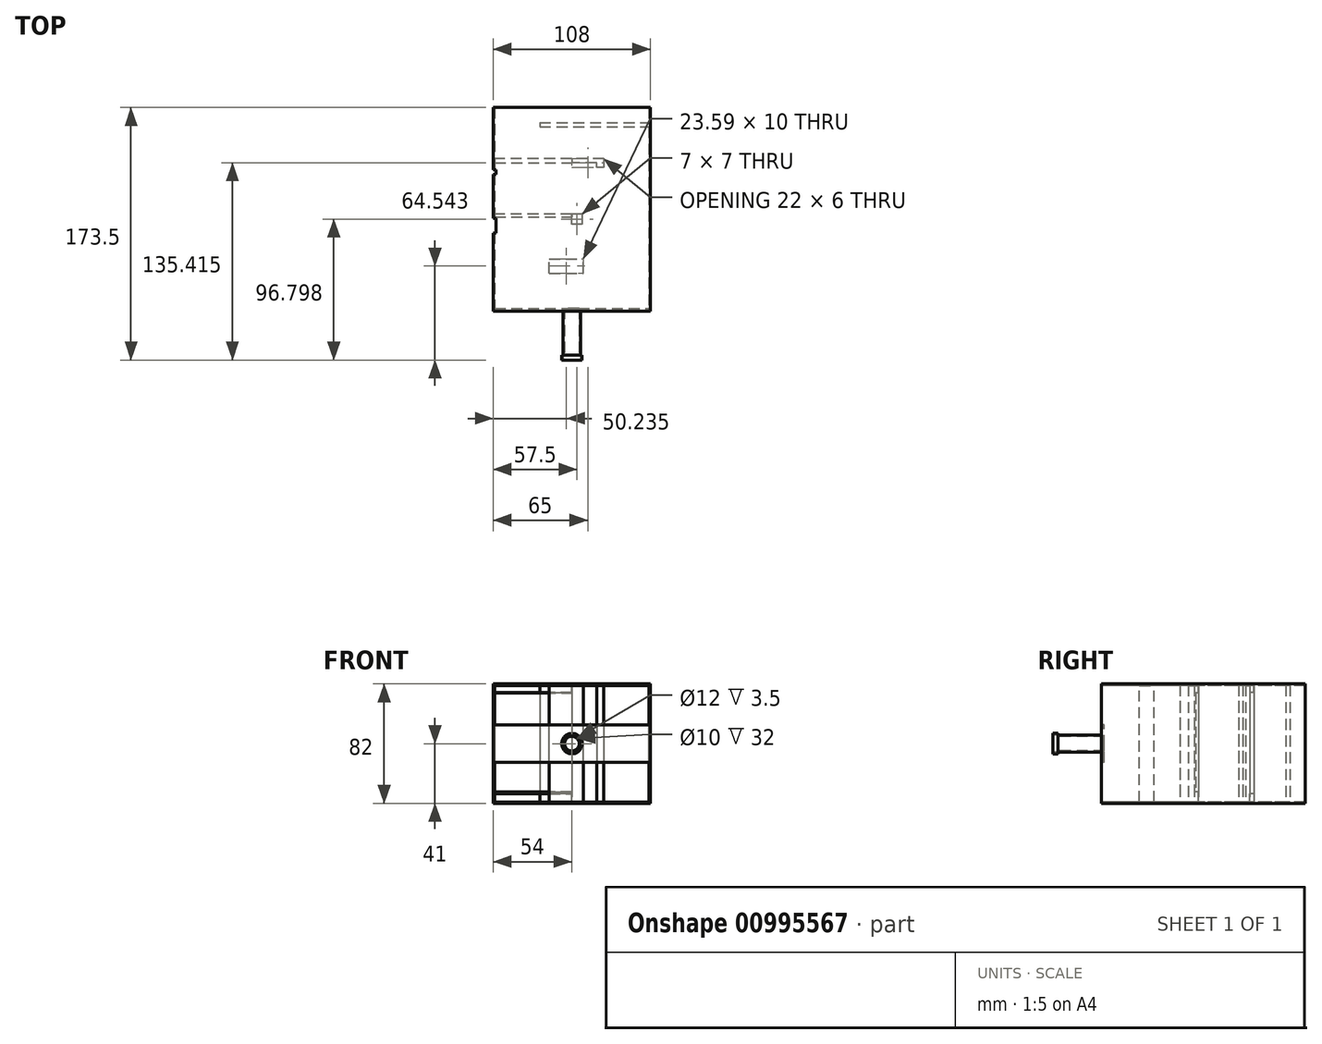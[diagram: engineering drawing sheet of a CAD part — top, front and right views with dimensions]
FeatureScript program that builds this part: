
annotation { "Feature Type Name" : "Feature", "Feature Type Description" : "" }
export const myFeature = defineFeature(function(context is Context, id is Id, definition is map)
    precondition{}
    {
        {
            var Q0;
            Q0=qCreatedBy(makeId("Front.planeOp"),FACE);
            var sketch = newSketch(context, id + "F0", { "sketchPlane" : qUnion([Q0])});
            skLineSegment(sketch, "E0.bottom", {"start": v(54, 41) * mm, "end": v(-54, 41) * mm});
            skLineSegment(sketch, "E0.top", {"start": v(54, -41) * mm, "end": v(-54, -41) * mm});
            skLineSegment(sketch, "E0.left", {"start": v(54, 41) * mm, "end": v(54, -41) * mm});
            skLineSegment(sketch, "E0.right", {"start": v(-54, 41) * mm, "end": v(-54, -41) * mm});
            skPoint(sketch, "E0.middle", {"position": v(0, 0) * mm});
            skSolve(sketch);
        }
        {
            var Q0;
            Q0=makeQuery(id+"F0.imprint","IMPRINT",FACE,{"disambiguationData":[TD([[makeQuery(id+"F0.imprint","IMPRINT",EDGE,{"derivedFrom":sQuery(id+"F0.wireOp",EDGE,"E0.bottom")}),1.0]])]});
            extrude(context, id + "F1", {"entities" : qUnion([Q0]), "depth" : 140 * mm, "offsetDistance" : 25 * mm});
        }
        {
            var Q0;
            Q0=makeQuery(id+"F1.opExtrude","CAP_FACE",FACE,{"disambiguationData":[OSD([sQuery(id+"F0.wireOp",EDGE,"E0.bottom"),sQuery(id+"F0.wireOp",EDGE,"E0.top"),sQuery(id+"F0.wireOp",EDGE,"E0.left"),sQuery(id+"F0.wireOp",EDGE,"E0.right")])],"isStart":false});
            var sketch = newSketch(context, id + "F2", { "sketchPlane" : qUnion([Q0])});
            skLineSegment(sketch, "E1.bottom", {"start": v(53, 40) * mm, "end": v(-53, 40) * mm});
            skLineSegment(sketch, "E1.top", {"start": v(53, -40) * mm, "end": v(-53, -40) * mm});
            skLineSegment(sketch, "E1.left", {"start": v(53, 40) * mm, "end": v(53, -40) * mm});
            skLineSegment(sketch, "E1.right", {"start": v(-53, 40) * mm, "end": v(-53, -40) * mm});
            skPoint(sketch, "E1.middle", {"position": v(0, 0) * mm});
            skSolve(sketch);
        }
        {
            var Q0;
            Q0 = qSketchRegion(id + "F2", true);
            extrude(context, id + "F3", {"entities" : qUnion([Q0]), "operationType" : NewBodyOperationType.REMOVE, "endBound" : BoundingType.UP_TO_NEXT, "oppositeDirection" : true, "depth" : 25 * mm, "offsetDistance" : 25 * mm});
        }
        {
            var Q0;
            Q0=makeQuery(id+"F3.boolean.opBoolean","COPY",FACE,{"derivedFrom":makeQuery(id+"F3.opExtrude","SWEPT_FACE",FACE,{"disambiguationData":[OSD([sQuery(id+"F2.wireOp",EDGE,"E1.right")])]})});
            var sketch = newSketch(context, id + "F4", { "sketchPlane" : qUnion([Q0])});
            skLineSegment(sketch, "E2.bottom", {"start": v(-75.2, 40) * mm, "end": v(-73.2, 40) * mm});
            skLineSegment(sketch, "E2.top", {"start": v(-75.2, -40) * mm, "end": v(-73.2, -40) * mm});
            skLineSegment(sketch, "E2.left", {"start": v(-75.2, 40) * mm, "end": v(-75.2, -40) * mm});
            skLineSegment(sketch, "E2.right", {"start": v(-73.2, 40) * mm, "end": v(-73.2, -40) * mm});
            skSolve(sketch);
        }
        {
            var Q0;
            Q0 = qSketchRegion(id + "F4", true);
            extrude(context, id + "F5", {"entities" : qUnion([Q0]), "operationType" : NewBodyOperationType.ADD, "depth" : 60 * mm, "offsetDistance" : 25 * mm});
        }
        {
            var Q0;
            Q0=makeQuery(id+"F5.opExtrude","SWEPT_FACE",FACE,{"disambiguationData":[OSD([sQuery(id+"F4.wireOp",EDGE,"E2.left")])]});
            var sketch = newSketch(context, id + "F6", { "sketchPlane" : qUnion([Q0])});
            skLineSegment(sketch, "E3.bottom", {"start": v(0, 40) * mm, "end": v(7, 40) * mm});
            skLineSegment(sketch, "E3.top", {"start": v(0, -40) * mm, "end": v(7, -40) * mm});
            skLineSegment(sketch, "E3.left", {"start": v(0, 40) * mm, "end": v(0, -40) * mm});
            skLineSegment(sketch, "E3.right", {"start": v(7, 40) * mm, "end": v(7, -40) * mm});
            skSolve(sketch);
        }
        {
            var Q0;
            Q0=makeQuery(id+"F6.imprint","IMPRINT",FACE,{"disambiguationData":[TD([[makeQuery(id+"F6.imprint","IMPRINT",EDGE,{"derivedFrom":sQuery(id+"F6.wireOp",EDGE,"E3.bottom")}),1.0]])]});
            extrude(context, id + "F7", {"entities" : qUnion([Q0]), "operationType" : NewBodyOperationType.ADD, "depth" : 5 * mm, "offsetDistance" : 25 * mm});
        }
        {
            var Q0;
            Q0=makeQuery(id+"F5.opExtrude","SWEPT_FACE",FACE,{"disambiguationData":[OSD([sQuery(id+"F4.wireOp",EDGE,"E2.left")])]});
            var sketch = newSketch(context, id + "F8", { "sketchPlane" : qUnion([Q0])});
            skLineSegment(sketch, "E4.bottom", {"start": v(0, 40) * mm, "end": v(-53, 40) * mm});
            skLineSegment(sketch, "E4.top", {"start": v(0, 34.75) * mm, "end": v(-53, 34.75) * mm});
            skLineSegment(sketch, "E4.left", {"start": v(0, 40) * mm, "end": v(0, 34.75) * mm});
            skLineSegment(sketch, "E4.right", {"start": v(-53, 40) * mm, "end": v(-53, 34.75) * mm});
            skSolve(sketch);
        }
        {
            var Q0;
            Q0=makeQuery(id+"F8.imprint","IMPRINT",FACE,{"disambiguationData":[TD([[makeQuery(id+"F8.imprint","IMPRINT",EDGE,{"derivedFrom":sQuery(id+"F8.wireOp",EDGE,"E4.bottom")}),1.0]])]});
            extrude(context, id + "F9", {"entities" : qUnion([Q0]), "operationType" : NewBodyOperationType.REMOVE, "oppositeDirection" : true, "depth" : 5 * mm, "offsetDistance" : 25 * mm});
        }
        {
            var Q0;
            Q0=makeQuery(id+"F5.opExtrude","SWEPT_FACE",FACE,{"disambiguationData":[OSD([sQuery(id+"F4.wireOp",EDGE,"E2.left")])]});
            var sketch = newSketch(context, id + "F10", { "sketchPlane" : qUnion([Q0])});
            skLineSegment(sketch, "E5.bottom", {"start": v(-53, -33.15) * mm, "end": v(0, -33.15) * mm});
            skLineSegment(sketch, "E5.top", {"start": v(-53, -40) * mm, "end": v(0, -40) * mm});
            skLineSegment(sketch, "E5.left", {"start": v(-53, -33.15) * mm, "end": v(-53, -40) * mm});
            skLineSegment(sketch, "E5.right", {"start": v(0, -33.15) * mm, "end": v(0, -40) * mm});
            skSolve(sketch);
        }
        {
            var Q0;
            Q0=makeQuery(id+"F10.imprint","IMPRINT",FACE,{"disambiguationData":[TD([[makeQuery(id+"F10.imprint","IMPRINT",EDGE,{"derivedFrom":sQuery(id+"F10.wireOp",EDGE,"E5.bottom")}),-1.0]])]});
            extrude(context, id + "F11", {"entities" : qUnion([Q0]), "operationType" : NewBodyOperationType.REMOVE, "oppositeDirection" : true, "depth" : 25 * mm, "offsetDistance" : 25 * mm});
        }
        {
            var Q0;
            Q0=makeQuery(id+"F1.opExtrude","SWEPT_FACE",FACE,{"disambiguationData":[OSD([sQuery(id+"F0.wireOp",EDGE,"E0.right")])]});
            var sketch = newSketch(context, id + "F12", { "sketchPlane" : qUnion([Q0])});
            skLineSegment(sketch, "E6.bottom", {"start": v(76.17, 41) * mm, "end": v(86.17, 41) * mm});
            skLineSegment(sketch, "E6.top", {"start": v(76.17, -41) * mm, "end": v(86.17, -41) * mm});
            skLineSegment(sketch, "E6.left", {"start": v(76.17, 41) * mm, "end": v(76.17, -41) * mm});
            skLineSegment(sketch, "E6.right", {"start": v(86.17, 41) * mm, "end": v(86.17, -41) * mm});
            skSolve(sketch);
        }
        {
            var Q0;
            Q0 = qSketchRegion(id + "F12", true);
            extrude(context, id + "F13", {"entities" : qUnion([Q0]), "operationType" : NewBodyOperationType.REMOVE, "oppositeDirection" : true, "depth" : 2 * mm, "offsetDistance" : 25 * mm});
        }
        {
            var Q0;
            {var subQ2=makeQuery(id+"F5.opExtrude","SWEPT_FACE",FACE,{"disambiguationData":[OSD([sQuery(id+"F4.wireOp",EDGE,"E2.left")])]});var subQ8=makeQuery(id+"F5.opExtrude","SWEPT_FACE",FACE,{"disambiguationData":[OSD([sQuery(id+"F4.wireOp",EDGE,"E2.right")])]});var subQ9=makeQuery(id+"F3.boolean.opBoolean","COPY",FACE,{"derivedFrom":makeQuery(id+"F3.opExtrude","SWEPT_FACE",FACE,{"disambiguationData":[OSD([sQuery(id+"F2.wireOp",EDGE,"E1.right")])]})});Q0=makeQuery(id+"F13.boolean.opBoolean","SPLIT",FACE,{"disambiguationData":[TD([subQ2])],"derivedFrom":makeQuery(id+"F11.boolean.opBoolean","MERGE",FACE,{"derivedFrom":[makeQuery(id+"F9.boolean.opBoolean","MERGE",FACE,{"derivedFrom":[makeQuery(id+"F5.boolean.opBoolean","SPLIT",FACE,{"disambiguationData":[TD([subQ2])],"derivedFrom":subQ9}),makeQuery(id+"F5.boolean.opBoolean","SPLIT",FACE,{"disambiguationData":[TD([subQ8])],"derivedFrom":subQ9})],"fromTools":[makeQuery(id+"F9.opExtrude","SWEPT_FACE",FACE,{"disambiguationData":[OSD([sQuery(id+"F8.wireOp",EDGE,"E4.right")])]})]})],"fromTools":[makeQuery(id+"F11.opExtrude","SWEPT_FACE",FACE,{"disambiguationData":[OSD([sQuery(id+"F10.wireOp",EDGE,"E5.left")])]})]})});}
            var sketch = newSketch(context, id + "F14", { "sketchPlane" : qUnion([Q0])});
            skLineSegment(sketch, "E7.bottom", {"start": v(-35.08, 40) * mm, "end": v(-38.08, 40) * mm});
            skLineSegment(sketch, "E7.top", {"start": v(-35.08, -40) * mm, "end": v(-38.08, -40) * mm});
            skLineSegment(sketch, "E7.left", {"start": v(-35.08, 40) * mm, "end": v(-35.08, -40) * mm});
            skLineSegment(sketch, "E7.right", {"start": v(-38.08, 40) * mm, "end": v(-38.08, -40) * mm});
            skSolve(sketch);
        }
        {
            var Q0;
            Q0 = qSketchRegion(id + "F14", true);
            extrude(context, id + "F15", {"entities" : qUnion([Q0]), "operationType" : NewBodyOperationType.ADD, "depth" : 75 * mm, "offsetDistance" : 25 * mm});
        }
        {
            var Q0;
            Q0=makeQuery(id+"F15.opExtrude","SWEPT_FACE",FACE,{"disambiguationData":[OSD([sQuery(id+"F14.wireOp",EDGE,"E7.right")])]});
            var sketch = newSketch(context, id + "F16", { "sketchPlane" : qUnion([Q0])});
            skLineSegment(sketch, "E8.bottom", {"start": v(17, 40) * mm, "end": v(22, 40) * mm});
            skLineSegment(sketch, "E8.top", {"start": v(17, -40) * mm, "end": v(22, -40) * mm});
            skLineSegment(sketch, "E8.left", {"start": v(17, 40) * mm, "end": v(17, -40) * mm});
            skLineSegment(sketch, "E8.right", {"start": v(22, 40) * mm, "end": v(22, -40) * mm});
            skSolve(sketch);
        }
        {
            var Q0;
            Q0 = qSketchRegion(id + "F16", true);
            extrude(context, id + "F17", {"entities" : qUnion([Q0]), "operationType" : NewBodyOperationType.ADD, "depth" : 3 * mm, "offsetDistance" : 25 * mm});
        }
        {
            var Q0;
            {var subQ4=makeQuery(id+"F13.opExtrude","SWEPT_FACE",FACE,{"disambiguationData":[OSD([sQuery(id+"F12.wireOp",EDGE,"E6.left")])]});var subQ5=sQuery(id+"F0.wireOp",EDGE,"E0.right");Q0=makeQuery(id+"FcwgyYnghoDdtHb_1.boolean.opBoolean","SPLIT",FACE,{"disambiguationData":[TD([makeQuery(id+"F13.boolean.opBoolean","COPY",FACE,{"derivedFrom":subQ4})])],"derivedFrom":makeQuery(id+"F13.boolean.opBoolean","SPLIT",FACE,{"disambiguationData":[TD([subQ4])],"derivedFrom":makeQuery(id+"F1.opExtrude","SWEPT_FACE",FACE,{"disambiguationData":[OSD([subQ5])]})})});}
            var sketch = newSketch(context, id + "F18", { "sketchPlane" : qUnion([Q0])});
            skLineSegment(sketch, "E9.bottom", {"start": v(42.88, 41) * mm, "end": v(45.88, 41) * mm});
            skLineSegment(sketch, "E9.top", {"start": v(42.88, -41) * mm, "end": v(45.88, -41) * mm});
            skLineSegment(sketch, "E9.left", {"start": v(42.88, 41) * mm, "end": v(42.88, -41) * mm});
            skLineSegment(sketch, "E9.right", {"start": v(45.88, 41) * mm, "end": v(45.88, -41) * mm});
            skSolve(sketch);
        }
        {
            var Q0;
            Q0=makeQuery(id+"F18.imprint","IMPRINT",FACE,{"disambiguationData":[TD([[makeQuery(id+"F18.imprint","IMPRINT",EDGE,{"derivedFrom":sQuery(id+"F18.wireOp",EDGE,"E9.bottom")}),1.0]])]});
            extrude(context, id + "F19", {"entities" : qUnion([Q0]), "operationType" : NewBodyOperationType.REMOVE, "oppositeDirection" : true, "depth" : 2 * mm, "offsetDistance" : 25 * mm});
        }
        {
            var Q0;
            Q0=makeQuery(id+"F15.opExtrude","SWEPT_FACE",FACE,{"disambiguationData":[OSD([sQuery(id+"F14.wireOp",EDGE,"E7.right")])]});
            var sketch = newSketch(context, id + "F20", { "sketchPlane" : qUnion([Q0])});
            skLineSegment(sketch, "E10.bottom", {"start": v(-53, -40) * mm, "end": v(0, -40) * mm});
            skLineSegment(sketch, "E10.top", {"start": v(-53, -34.3) * mm, "end": v(0, -34.3) * mm});
            skLineSegment(sketch, "E10.left", {"start": v(-53, -40) * mm, "end": v(-53, -34.3) * mm});
            skLineSegment(sketch, "E10.right", {"start": v(0, -40) * mm, "end": v(0, -34.3) * mm});
            skLineSegment(sketch, "E11.bottom", {"start": v(-53, 40) * mm, "end": v(0, 40) * mm});
            skLineSegment(sketch, "E11.top", {"start": v(-53, 35.08) * mm, "end": v(0, 35.08) * mm});
            skLineSegment(sketch, "E11.left", {"start": v(-53, 40) * mm, "end": v(-53, 35.08) * mm});
            skLineSegment(sketch, "E11.right", {"start": v(0, 40) * mm, "end": v(0, 35.08) * mm});
            skSolve(sketch);
        }
        {
            var Q0;
            Q0 = qSketchRegion(id + "F20", true);
            extrude(context, id + "F21", {"entities" : qUnion([Q0]), "operationType" : NewBodyOperationType.REMOVE, "oppositeDirection" : true, "depth" : 25 * mm, "offsetDistance" : 25 * mm});
        }
        {
            var Q0;
            Q0=makeQuery(id+"F3.boolean.opBoolean","COPY",FACE,{"derivedFrom":makeQuery(id+"F3.opExtrude","SWEPT_FACE",FACE,{"disambiguationData":[OSD([sQuery(id+"F2.wireOp",EDGE,"E1.left")])]})});
            var sketch = newSketch(context, id + "F22", { "sketchPlane" : qUnion([Q0])});
            skLineSegment(sketch, "E12.bottom", {"start": v(10.42, 40) * mm, "end": v(13.42, 40) * mm});
            skLineSegment(sketch, "E12.top", {"start": v(10.42, -40) * mm, "end": v(13.42, -40) * mm});
            skLineSegment(sketch, "E12.left", {"start": v(10.42, 40) * mm, "end": v(10.42, -40) * mm});
            skLineSegment(sketch, "E12.right", {"start": v(13.42, 40) * mm, "end": v(13.42, -40) * mm});
            skSolve(sketch);
        }
        {
            var Q0;
            Q0 = qSketchRegion(id + "F22", true);
            extrude(context, id + "F23", {"entities" : qUnion([Q0]), "operationType" : NewBodyOperationType.ADD, "depth" : 75 * mm, "offsetDistance" : 25 * mm});
        }
        {
            var Q0;
            Q0=makeQuery(id+"F21.boolean.opBoolean","MERGE",FACE,{"derivedFrom":[makeQuery(id+"F9.boolean.opBoolean","MERGE",FACE,{"derivedFrom":[makeQuery(id+"F3.boolean.opBoolean","COPY",FACE,{"derivedFrom":makeQuery(id+"F3.opExtrude","SWEPT_FACE",FACE,{"disambiguationData":[OSD([sQuery(id+"F2.wireOp",EDGE,"E1.bottom")])]})})],"fromTools":[makeQuery(id+"F9.opExtrude","SWEPT_FACE",FACE,{"disambiguationData":[OSD([sQuery(id+"F8.wireOp",EDGE,"E4.bottom")])]})]})],"fromTools":[makeQuery(id+"F21.opExtrude","SWEPT_FACE",FACE,{"disambiguationData":[OSD([sQuery(id+"F20.wireOp",EDGE,"E11.bottom")])]})]});
            var sketch = newSketch(context, id + "F24", { "sketchPlane" : qUnion([Q0])});
            skLineSegment(sketch, "E13.bottom", {"start": v(-15.56, 113.96) * mm, "end": v(8.03, 113.96) * mm});
            skLineSegment(sketch, "E13.top", {"start": v(-15.56, 103.96) * mm, "end": v(8.03, 103.96) * mm});
            skLineSegment(sketch, "E13.left", {"start": v(-15.56, 113.96) * mm, "end": v(-15.56, 103.96) * mm});
            skLineSegment(sketch, "E13.right", {"start": v(8.03, 113.96) * mm, "end": v(8.03, 103.96) * mm});
            skSolve(sketch);
        }
        {
            var Q0;
            Q0 = qSketchRegion(id + "F24", true);
            extrude(context, id + "F25", {"entities" : qUnion([Q0]), "operationType" : NewBodyOperationType.ADD, "endBound" : BoundingType.UP_TO_NEXT, "depth" : 25 * mm, "offsetDistance" : 25 * mm});
        }
        {
            var Q0;
            Q0=makeQuery(id+"F1.opExtrude","CAP_FACE",FACE,{"disambiguationData":[OSD([sQuery(id+"F0.wireOp",EDGE,"E0.bottom"),sQuery(id+"F0.wireOp",EDGE,"E0.top"),sQuery(id+"F0.wireOp",EDGE,"E0.left"),sQuery(id+"F0.wireOp",EDGE,"E0.right")])],"isStart":false});
            var sketch = newSketch(context, id + "F26", { "sketchPlane" : qUnion([Q0])});
            skLineSegment(sketch, "E14.bottom", {"start": v(-54, 13) * mm, "end": v(54, 13) * mm});
            skLineSegment(sketch, "E14.top", {"start": v(-54, -13) * mm, "end": v(54, -13) * mm});
            skLineSegment(sketch, "E14.left", {"start": v(-54, 13) * mm, "end": v(-54, -13) * mm});
            skLineSegment(sketch, "E14.right", {"start": v(54, 13) * mm, "end": v(54, -13) * mm});
            skSolve(sketch);
        }
        {
            var Q0;
            {var subQ0=sQuery(id+"F26.wireOp",EDGE,"E14.bottom");var subQ1=makeQuery(id+"F3.boolean.opBoolean","COPY",EDGE,{"derivedFrom":makeQuery(id+"F3.opExtrude","CAP_EDGE",EDGE,{"disambiguationData":[OSD([sQuery(id+"F2.wireOp",EDGE,"E1.right")])],"isStart":true})});var subQ2=makeQuery(id+"F26.imprint","INTERSECT",VERTEX,{"derivedFrom":[subQ1,subQ0]});Q0=makeQuery(id+"F26.imprint","IMPRINT",FACE,{"disambiguationData":[TD([[makeQuery(id+"F26.imprint","IMPRINT",EDGE,{"disambiguationData":[TD([[subQ2,-1.0]])],"derivedFrom":subQ0}),-1.0]])]});}
            extrude(context, id + "F27", {"entities" : qUnion([Q0]), "operationType" : NewBodyOperationType.ADD, "oppositeDirection" : true, "depth" : 2 * mm, "offsetDistance" : 25 * mm});
        }
        {
            var Q0;
            Q0=makeQuery(id+"F27.boolean.opBoolean","MERGE",FACE,{"derivedFrom":[makeQuery(id+"F1.opExtrude","CAP_FACE",FACE,{"disambiguationData":[OSD([sQuery(id+"F0.wireOp",EDGE,"E0.bottom"),sQuery(id+"F0.wireOp",EDGE,"E0.top"),sQuery(id+"F0.wireOp",EDGE,"E0.left"),sQuery(id+"F0.wireOp",EDGE,"E0.right")])],"isStart":false}),makeQuery(id+"F27.opExtrude","CAP_FACE",FACE,{"disambiguationData":[OSD([sQuery(id+"F2.wireOp",EDGE,"E1.left"),sQuery(id+"F2.wireOp",EDGE,"E1.right"),sQuery(id+"F26.wireOp",EDGE,"E14.bottom"),sQuery(id+"F26.wireOp",EDGE,"E14.top")])],"isStart":true})]});
            var sketch = newSketch(context, id + "F28", { "sketchPlane" : qUnion([Q0])});
            skCircle(sketch, "E15", {"center": v(0, 0) * mm, "radius": 6 * mm});
            skSolve(sketch);
        }
        {
            var Q0;
            Q0 = qSketchRegion(id + "F28", true);
            extrude(context, id + "F29", {"entities" : qUnion([Q0]), "operationType" : NewBodyOperationType.ADD, "depth" : 30 * mm, "offsetDistance" : 25 * mm});
        }
        {
            var Q0;
            Q0=makeQuery(id+"F29.opExtrude","CAP_FACE",FACE,{"disambiguationData":[OSD([sQuery(id+"F28.wireOp",EDGE,"E15")])],"isStart":false});
            var sketch = newSketch(context, id + "F30", { "sketchPlane" : qUnion([Q0])});
            skCircle(sketch, "E16", {"center": v(0, 0) * mm, "radius": 5 * mm});
            skSolve(sketch);
        }
        {
            var Q0;
            Q0=makeQuery(id+"F30.imprint","IMPRINT",FACE,{"disambiguationData":[TD([[makeQuery(id+"F30.imprint","IMPRINT",EDGE,{"derivedFrom":sQuery(id+"F30.wireOp",EDGE,"E16")}),1.0]])]});
            extrude(context, id + "F31", {"entities" : qUnion([Q0]), "operationType" : NewBodyOperationType.REMOVE, "oppositeDirection" : true, "depth" : 40 * mm, "offsetDistance" : 25 * mm});
        }
        {
            var Q0;
            Q0=makeQuery(id+"F29.opExtrude","CAP_FACE",FACE,{"disambiguationData":[OSD([sQuery(id+"F28.wireOp",EDGE,"E15")])],"isStart":false});
            var sketch = newSketch(context, id + "F32", { "sketchPlane" : qUnion([Q0])});
            skCircle(sketch, "E17", {"center": v(0, 0) * mm, "radius": 7 * mm});
            skSolve(sketch);
        }
        {
            var Q0;
            Q0 = qSketchRegion(id + "F32", true);
            extrude(context, id + "F33", {"entities" : qUnion([Q0]), "operationType" : NewBodyOperationType.ADD, "depth" : 3.5 * mm, "offsetDistance" : 25 * mm});
        }
        {
            var Q0;
            Q0=makeQuery(id+"F33.opExtrude","CAP_FACE",FACE,{"disambiguationData":[OSD([sQuery(id+"F32.wireOp",EDGE,"E17")])],"isStart":false});
            var sketch = newSketch(context, id + "F34", { "sketchPlane" : qUnion([Q0])});
            skCircle(sketch, "E18", {"center": v(0, 0) * mm, "radius": 6 * mm});
            skSolve(sketch);
        }
        {
            var Q0;
            Q0 = qSketchRegion(id + "F34", true);
            extrude(context, id + "F35", {"entities" : qUnion([Q0]), "operationType" : NewBodyOperationType.REMOVE, "oppositeDirection" : true, "depth" : 3.5 * mm, "offsetDistance" : 25 * mm});
        }
    });
